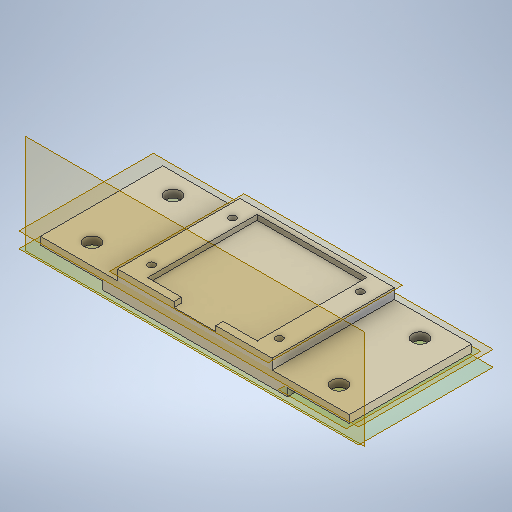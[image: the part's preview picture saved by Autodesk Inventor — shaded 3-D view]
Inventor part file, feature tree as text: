
AUTODESK INVENTOR PART (.ipt)
format: ipt  version: 2025.2 (Build 292293000, 293)  size: 527,360 bytes
history: native  units: mm
features: sketch x8, other x6, extrude x6, hole x2
ambient origin geometry x8: Origin, YZ Plane, XZ Plane, XY Plane, X Axis, Y Axis, Z Axis, Center Point
bodies: Body1 (feature_tree)
feature tree (22):
  other  "ソリッド1"
  extrude  "押し出し1"  Depth=120.0mm
  other  "作業平面1"
  other  "作業平面2"
  extrude  "押し出し3"  Depth=47.5mm
  other  "作業平面3"
  extrude  "押し出し4"  Depth=6.0mm TaperAngle=0.0deg
  extrude  "押し出し5"  TaperAngle=0.0deg  [1 undecoded]
  hole  "穴1"  [1 undecoded]
  extrude  "押し出し6"  Depth=60.0mm
  other  "作業平面4"
  extrude  "押し出し7"  Depth=4.0mm TaperAngle=0.0deg
  other  "作業平面5"
  hole  "穴2"  [1 undecoded]
  sketch  "スケッチ1"
  sketch  "スケッチ3"
  sketch  "スケッチ4"
  sketch  "スケッチ5"
  sketch  "スケッチ6"
  sketch  "スケッチ7"
  sketch  "スケッチ8"
  sketch  "スケッチ9"
note: 3 required parameter values undecoded (feature->parameter linkage not recoverable at this tier; creation-order binding heuristic only, values carry confidence <= 0.55)
